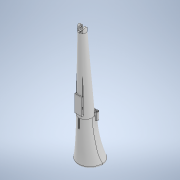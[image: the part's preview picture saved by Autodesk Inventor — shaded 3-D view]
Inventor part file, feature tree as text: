
AUTODESK INVENTOR PART (.ipt)
format: ipt  version: 2021 (Build 250183000, 183)  size: 909,824 bytes
history: native  units: mm
features: sketch x37, extrude x22, plane x17, fillet x4, hole x3, loft x2, revolve x2, other x1, thread x1
ambient origin geometry x8: Origin, YZ Plane, XZ Plane, XY Plane, X Axis, Y Axis, Z Axis, Center Point
bodies: Body1 (feature_tree)
feature tree (89):
  other  "Sólido1"
  plane  "Plano de trabajo1"
  plane  "Plano de trabajo2"
  plane  "Plano de trabajo4"
  plane  "Plano de trabajo5"
  plane  "Plano de trabajo6"
  sketch  "Boceto1"  dims[d1=250.0mm d2=0.0mm d3=-80.0mm d4=-110.0mm]
  sketch  "Boceto2"  dims[d5=-140.0mm d7=-0.0mm d8=2.0mm]
  sketch  "Boceto3"  dims[d9=140.0mm d10=250.0mm]
  sketch  "Boceto4"  dims[d11=24.0mm d22=0.0mm d23=90.0deg d24=0.0mm d25=90.0deg]
  sketch  "Boceto6"  dims[d44=45.0mm d49=29.11157mm]
  sketch  "Boceto7"  dims[d50=29.11157mm d53=29.11157mm]
  loft  "Solevación1"
  fillet  "Empalme2"  [1 undecoded]
  extrude  "Extrusión1"  TaperAngle=0.0deg  [1 undecoded]
  fillet  "Empalme5"  Radius=2.0mm
  plane  "Plano de trabajo7"
  extrude  "Extrusión2"  Depth=250.0mm
  plane  "Plano de trabajo8"
  plane  "Plano de trabajo9"
  loft  "Solevación9"
  plane  "Plano de trabajo10"
  extrude  "Extrusión3"  Depth=29.11157mm
  plane  "Plano de trabajo11"
  revolve  "Revolución1"  [1 undecoded]
  revolve  "Revolución2"  [1 undecoded]
  extrude  "Extrusión4"  Depth=32.5mm
  plane  "Plano de trabajo12"
  extrude  "Extrusión5"  Depth=44.747934mm
  plane  "Plano de trabajo13"
  plane  "Plano de trabajo14"
  extrude  "Extrusión6"  Depth=42.747934mm
  extrude  "Extrusión7"  Depth=42.747934mm
  extrude  "Extrusión8"  Depth=13.0mm
  extrude  "Extrusión11"  Depth=7.75mm
  extrude  "Extrusión9"  Depth=7.75mm
  extrude  "Extrusión10"  Depth=16.0mm
  extrude  "Extrusión12"  Depth=12.0mm
  sketch  "Boceto30"  dims[d160=-19.75mm d161=0.0mm]
  extrude  "Extrusión13"  Depth=7.75mm
  extrude  "Extrusión14"  Depth=7.75mm
  extrude  "Extrusión15"  TaperAngle=0.0deg  [1 undecoded]
  hole  "Agujero1"  [1 undecoded]
  thread  "Rosca1"  [1 undecoded]
  extrude  "Extrusión16"  Depth=2.0mm
  plane  "Plano de trabajo16"
  extrude  "Extrusión17"  TaperAngle=0.0deg  [1 undecoded]
  extrude  "Extrusión18"  TaperAngle=0.0deg  [1 undecoded]
  plane  "Plano de trabajo17"
  sketch  "Boceto46"  dims[d182=0.25mm]
  hole  "Agujero2"  [1 undecoded]
  hole  "Agujero3"  [1 undecoded]
  plane  "Plano de trabajo19"
  sketch  "Boceto50"  dims[d185=2.0mm]
  sketch  "Boceto45"  dims[d181=0.75mm]
  extrude  "Extrusión22"  Depth=12.0mm
  extrude  "Extrusión23"  [1 undecoded]
  extrude  "Extrusión24"  Depth=0.75mm
  plane  "Plano de trabajo20"
  extrude  "Extrusión25"  Depth=1.0mm
  fillet  "Empalme6"  Radius=11.0mm
  fillet  "Empalme7"  Radius=17.453293mm
  sketch  "Boceto44"  dims[d180=0.75mm]
  sketch  "Boceto47"  dims[d183=1.0mm]
  sketch  "Boceto49"  dims[d184=0.25mm]
  sketch  "Boceto9"  dims[d59=29.11157mm d61=29.11157mm]
  sketch  "Boceto10"  dims[d65=22.5mm d66=32.5mm]
  sketch  "Boceto15"  dims[d67=22.5mm d90=44.747934mm]
  sketch  "Boceto16"  dims[d91=42.747934mm d93=42.747934mm]
  sketch  "Boceto17"  dims[d96=0.0mm d97=90.0deg d98=0.0mm d99=90.0deg d100=0.0mm d101=90.0deg d102=0.0mm d103=90.0deg d112=42.747934mm]
  sketch  "Boceto18"  dims[d115=5.0mm d120=13.0mm]
  sketch  "Boceto19"  dims[d121=6.5mm d124=7.75mm]
  sketch  "Boceto20"  dims[d125=7.75mm d126=7.75mm]
  sketch  "Boceto21"  dims[d127=7.75mm d130=16.0mm]
  sketch  "Boceto22"  dims[d131=0.0mm d132=12.0mm]
  sketch  "Boceto24"  dims[d133=12.0mm d134=7.75mm]
  sketch  "Boceto25"  dims[d135=6.5mm d136=7.75mm]
  sketch  "Boceto26"  dims[d137=15.0mm d138=0.0mm]
  sketch  "Boceto27"  dims[d146=-8.5mm d147=30.0mm d148=2.0mm]
  sketch  "Boceto28"  dims[d149=25.12mm d150=2.0mm]
  sketch  "Boceto29"  dims[d151=10.357mm d156=0.0mm d157=90.0deg d158=0.0mm d159=90.0deg]
  sketch  "Boceto31"  dims[d163=0.0mm d164=2.0mm]
  sketch  "Boceto36"  dims[d165=15.0mm d166=4.0mm]
  sketch  "Boceto37"  dims[d167=30.0mm d168=12.0mm]
  sketch  "Boceto38"  dims[d169=0.0mm d170=-7.25mm]
  sketch  "Boceto39"  dims[d171=4.5mm d172=0.75mm]
  sketch  "Boceto40"  dims[d173=2.5mm d174=1.0mm d176=11.0mm d177=17.453293mm]
  sketch  "Boceto41"  dims[d179=2.939597mm]
  sketch  "Boceto51"  dims[d187=1.0mm d189=3.0mm d190=2.0mm d191=2.0mm d192=0.25mm d193=0.25mm d194=90.0deg d196=4.381635mm d197=0.0mm d198=-48.35mm d199=12.0mm d200=20.0mm d201=9.0mm d202=9.0mm d203=2.0mm d204=201.65mm d205=0.0mm d206=0.5mm d207=0.25mm d208=-7.5mm d209=100.0mm d210=0.0mm d211=35.0mm d212=0.0mm d213=210.0mm d214=0.0mm d215=2.0mm d216=1.059493mm d217=6.5mm d218=1.059493mm d219=5.0mm d220=2.0mm d221=0.0mm d222=2.0mm d223=6.5mm d224=1.059493mm d225=5.0mm d226=4.85mm d227=2.0mm d228=0.0mm d229=6.0mm d230=10.0mm d231=3.0mm d232=11.0mm d233=10.5mm d235=30.0deg d236=4.75mm d237=0.0mm d238=-17.0mm d239=100.0mm d240=0.0mm d241=6.5mm d242=1.65mm d243=3.3mm d244=15.6mm d245=2.0mm d247=16.0mm d248=2.0mm d249=0.0mm d250=4.5mm d251=0.75mm d252=2.5mm d253=1.0mm d254=11.0mm d255=17.453293mm d256=2.939597mm d257=0.75mm d258=0.75mm d259=0.25mm d260=1.0mm d261=0.25mm d262=2.0mm d263=1.0mm d264=3.0mm d265=2.0mm d266=2.0mm d267=0.25mm d268=0.25mm d269=40.0mm d270=1.0mm d271=1.0mm d272=7.75mm d273=0.5mm d274=8.5mm d275=90.0deg d276=0.0mm d277=17.75mm d280=22.5mm d281=2.0mm d282=0.0mm d283=0.0mm d292=2.0mm d293=0.0mm d296=3.5mm d297=0.0mm d299=4.0mm d300=3.708mm d301=3.023mm d302=2.0mm d303=14.3117mm d304=16.0mm d305=0.0mm d306=16.0mm d307=0.0mm d314=6.0mm d315=19.2mm d316=6.0mm d317=19.2mm d318=13.0mm d320=6.0mm d321=19.2mm d322=13.0mm d323=6.0mm d324=19.2mm d325=13.0mm d326=7.0mm d332=10.0mm d333=0.0mm d335=-41.6mm d336=4.0mm d337=1.0mm d338=9.0mm d339=4.0mm d340=1.0mm d341=9.0mm d342=4.0mm d343=5.2mm d344=6.0mm d345=0.0mm d346=15.0mm d347=5.0mm d349=5.0mm d351=0.0mm d352=45.0mm d354=10.0mm d355=10.0mm d356=0.0mm d357=15.0mm d358=0.0mm d359=2.0mm d363=50.4125mm d376=14.059493mm d377=2.0mm d378=0.0mm d379=2.0mm d380=11.25mm d381=90.0mm d382=290.0mm d383=14.059493mm d384=100.825mm d390=30.940507mm d391=2.0mm d392=100.825mm d393=14.790546mm d394=2.0mm d395=3.0mm d396=6.0mm d397=4.0mm d398=4.0mm d399=4.0mm d400=8.128453mm d401=12.0mm d402=4.45mm d403=2.5mm d404=1.65mm d405=1.65mm d406=1.0mm d407=2.0mm d408=2.0mm d409=0.0mm d411=50.4125mm d412=6.0mm d418=13.059493mm d419=6.5mm d420=6.5mm d421=50.4125mm d422=126.03125mm d423=0.0mm d424=15.0mm d425=5.0mm d426=5.0mm d427=0.0mm d428=45.0mm d429=10.0mm d430=2.0mm d431=4.0mm d432=6.0mm d433=8.0mm d434=2.0mm d435=90.0deg d436=20.0mm d437=0.0mm d438=4.0mm d439=6.0mm d440=8.0mm d441=2.0mm d442=90.0deg d443=20.0mm d444=0.0mm d446=10.0mm d447=3.0mm d448=11.5mm d450=9.0mm d451=9.0mm d452=90.0mm d453=750.0mm d454=22.5mm d455=43.0mm d456=44.0mm d457=14.059493mm d458=11.25mm d461=22.5mm d462=43.0mm d463=7.059493mm d464=3.0mm d465=6.0mm d466=3.0mm d467=6.0mm d468=45.0mm d469=130.0mm d470=17.04mm d471=30.0mm d472=15.0mm d473=1.5mm d474=1.5mm d475=2.0mm d476=1.5mm d477=2.0mm d478=120.0mm d479=0.0mm d480=120.0mm d481=0.0mm d482=116.0mm d483=0.0mm d484=69.0mm d485=0.0mm d486=-3.0mm d487=65.395511mm d488=2.6mm d489=60.0deg d490=45.0deg d491=15.0mm d492=1.6mm d493=0.0mm]
note: 12 required parameter values undecoded (feature->parameter linkage not recoverable at this tier; creation-order binding heuristic only, values carry confidence <= 0.55)